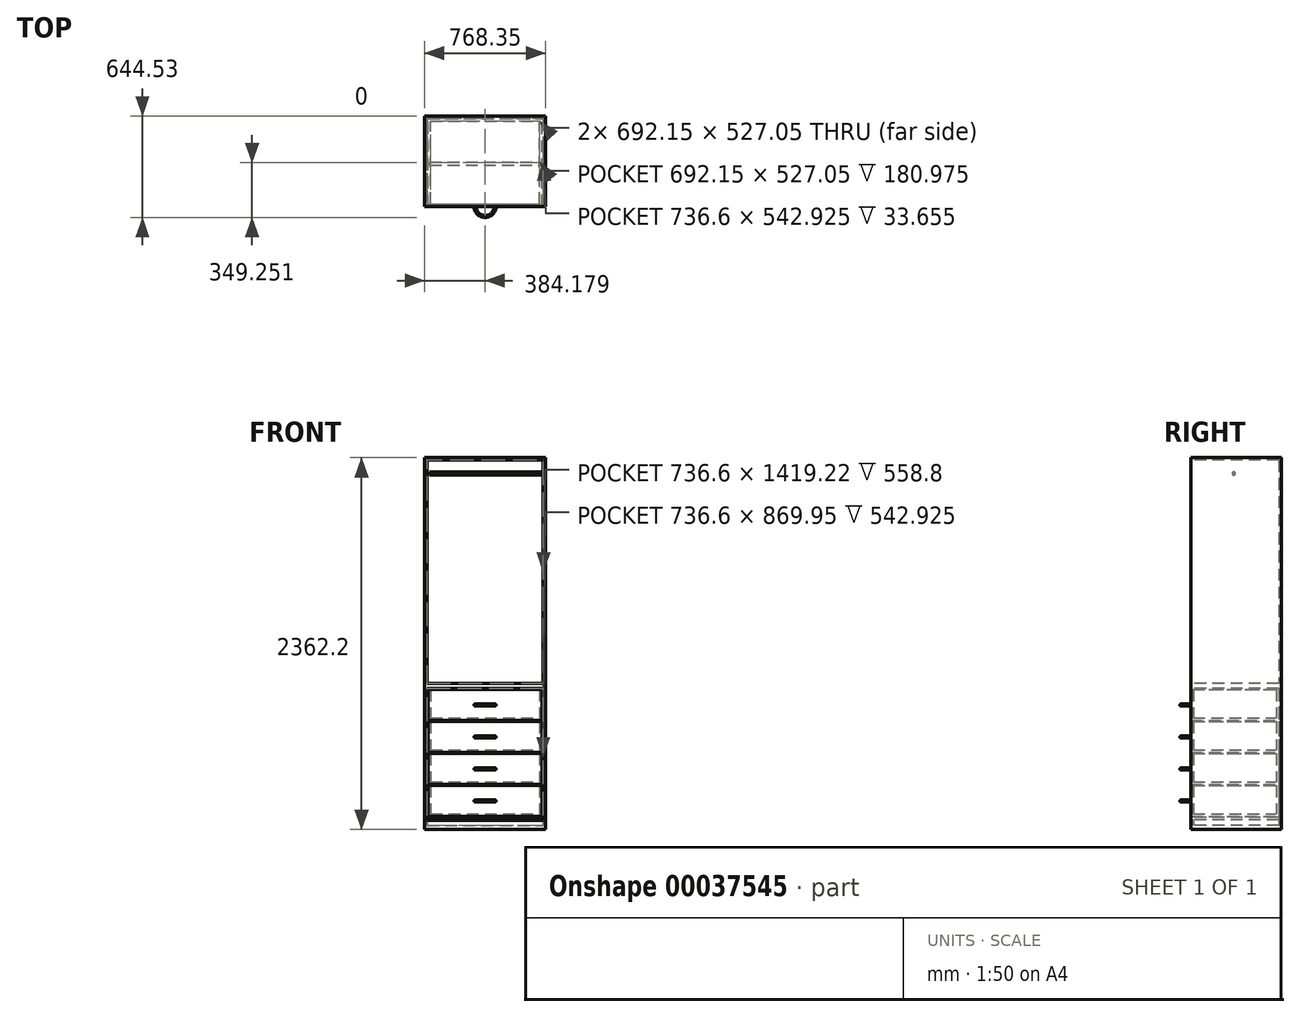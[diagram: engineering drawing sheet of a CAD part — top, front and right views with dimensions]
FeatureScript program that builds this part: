
annotation { "Feature Type Name" : "Feature", "Feature Type Description" : "" }
export const myFeature = defineFeature(function(context is Context, id is Id, definition is map)
    precondition{}
    {
        {
            var Q0;
            Q0=qCreatedBy(makeId("Top.planeOp"),FACE);
            var sketch = newSketch(context, id + "F0", { "sketchPlane" : qUnion([Q0])});
            skLineSegment(sketch, "E0.bottom", {"start": v(-263.66, 331.87) * mm, "end": v(504.7, 331.87) * mm});
            skLineSegment(sketch, "E0.top", {"start": v(-263.66, -242.8) * mm, "end": v(504.7, -242.8) * mm});
            skLineSegment(sketch, "E0.left", {"start": v(-263.66, 331.87) * mm, "end": v(-263.66, -242.8) * mm});
            skLineSegment(sketch, "E0.right", {"start": v(504.7, 331.87) * mm, "end": v(504.7, -242.8) * mm});
            skLineSegment(sketch, "E1.0", {"start": v(488.82, 317.59) * mm, "end": v(488.82, -257.09) * mm});
            skLineSegment(sketch, "E2.0", {"start": v(-247.78, 316) * mm, "end": v(504.7, 316) * mm});
            skLineSegment(sketch, "E3.0", {"start": v(-247.78, 331.87) * mm, "end": v(-247.78, -242.8) * mm});
            skLineSegment(sketch, "E4.0", {"start": v(-247.78, -226.93) * mm, "end": v(504.7, -226.93) * mm});
            skLineSegment(sketch, "E5.bottom", {"start": v(-263.66, 331.87) * mm, "end": v(-545.72, 331.87) * mm});
            skLineSegment(sketch, "E5.top", {"start": v(-263.66, -242.8) * mm, "end": v(-545.72, -242.8) * mm});
            skLineSegment(sketch, "E5.right", {"start": v(-545.72, 331.87) * mm, "end": v(-545.72, -242.8) * mm});
            skSolve(sketch);
        }
        {
            var Q0;
            {var subQ0=sQuery(id+"F0.wireOp",EDGE,"E2.0");var subQ3=sQuery(id+"F0.wireOp",EDGE,"E0.left");var subQ4=makeQuery(id+"F0.imprint","INTERSECT",VERTEX,{"derivedFrom":[subQ3,subQ0]});Q0=makeQuery(id+"F0.imprint","IMPRINT",FACE,{"disambiguationData":[TD([[makeQuery(id+"F0.imprint","IMPRINT",EDGE,{"disambiguationData":[TD([[subQ4,-1.0]])],"derivedFrom":subQ3}),1.0]])]});}
            var Q1;
            {var subQ3=sQuery(id+"F0.wireOp",EDGE,"E0.left");var subQ5=sQuery(id+"F0.wireOp",EDGE,"E0.bottom");var subQ6=makeQuery(id+"F0.imprint","INTERSECT",VERTEX,{"derivedFrom":[subQ5,subQ3]});Q1=makeQuery(id+"F0.imprint","IMPRINT",FACE,{"disambiguationData":[TD([[makeQuery(id+"F0.imprint","IMPRINT",EDGE,{"disambiguationData":[TD([[subQ6,-1.0]])],"derivedFrom":subQ5}),-1.0]])]});}
            var Q2;
            {var subQ3=sQuery(id+"F0.wireOp",EDGE,"E0.left");var subQ5=sQuery(id+"F0.wireOp",EDGE,"E0.top");var subQ7=makeQuery(id+"F0.imprint","INTERSECT",VERTEX,{"derivedFrom":[subQ5,subQ3]});Q2=makeQuery(id+"F0.imprint","IMPRINT",FACE,{"disambiguationData":[TD([[makeQuery(id+"F0.imprint","IMPRINT",EDGE,{"disambiguationData":[TD([[subQ7,-1.0]])],"derivedFrom":subQ5}),1.0]])]});}
            extrude(context, id + "F1", {"entities" : qUnion([Q0, Q1, Q2]), "depth" : 2362.2 * mm});
        }
        {
            var Q0;
            {var subQ0=sQuery(id+"F0.wireOp",EDGE,"E1.0");var subQ3=sQuery(id+"F0.wireOp",EDGE,"E0.bottom");var subQ4=makeQuery(id+"F0.imprint","INTERSECT",VERTEX,{"derivedFrom":[subQ3,subQ0]});Q0=makeQuery(id+"F0.imprint","IMPRINT",FACE,{"disambiguationData":[TD([[makeQuery(id+"F0.imprint","IMPRINT",EDGE,{"disambiguationData":[TD([[subQ4,1.0]])],"derivedFrom":subQ3}),-1.0]])]});}
            extrude(context, id + "F2", {"entities" : qUnion([Q0]), "operationType" : NewBodyOperationType.ADD, "depth" : 2362.2 * mm});
        }
        {
            var Q0;
            {var subQ3=sQuery(id+"F0.wireOp",EDGE,"E0.bottom");var subQ5=sQuery(id+"F0.wireOp",EDGE,"E0.right");var subQ7=makeQuery(id+"F0.imprint","INTERSECT",VERTEX,{"derivedFrom":[subQ3,subQ5]});Q0=makeQuery(id+"F0.imprint","IMPRINT",FACE,{"disambiguationData":[TD([[makeQuery(id+"F0.imprint","IMPRINT",EDGE,{"disambiguationData":[TD([[subQ7,1.0]])],"derivedFrom":subQ3}),-1.0]])]});}
            var Q1;
            {var subQ3=sQuery(id+"F0.wireOp",EDGE,"E0.right");var subQ5=sQuery(id+"F0.wireOp",EDGE,"E2.0");var subQ7=makeQuery(id+"F0.imprint","INTERSECT",VERTEX,{"derivedFrom":[subQ3,subQ5]});Q1=makeQuery(id+"F0.imprint","IMPRINT",FACE,{"disambiguationData":[TD([[makeQuery(id+"F0.imprint","IMPRINT",EDGE,{"disambiguationData":[TD([[subQ7,-1.0]])],"derivedFrom":subQ3}),-1.0]])]});}
            var Q2;
            {var subQ3=sQuery(id+"F0.wireOp",EDGE,"E0.right");var subQ5=sQuery(id+"F0.wireOp",EDGE,"E0.top");var subQ7=makeQuery(id+"F0.imprint","INTERSECT",VERTEX,{"derivedFrom":[subQ5,subQ3]});Q2=makeQuery(id+"F0.imprint","IMPRINT",FACE,{"disambiguationData":[TD([[makeQuery(id+"F0.imprint","IMPRINT",EDGE,{"disambiguationData":[TD([[subQ7,1.0]])],"derivedFrom":subQ5}),1.0]])]});}
            extrude(context, id + "F3", {"entities" : qUnion([Q0, Q1, Q2]), "operationType" : NewBodyOperationType.ADD, "depth" : 2362.2 * mm});
        }
        {
            var Q0;
            {var subQ0=sQuery(id+"F0.wireOp",EDGE,"E1.0");var subQ3=sQuery(id+"F0.wireOp",EDGE,"E0.top");var subQ4=makeQuery(id+"F0.imprint","INTERSECT",VERTEX,{"derivedFrom":[subQ3,subQ0]});Q0=makeQuery(id+"F0.imprint","IMPRINT",FACE,{"disambiguationData":[TD([[makeQuery(id+"F0.imprint","IMPRINT",EDGE,{"disambiguationData":[TD([[subQ4,1.0]])],"derivedFrom":subQ3}),1.0]])]});}
            extrude(context, id + "F4", {"entities" : qUnion([Q0]), "operationType" : NewBodyOperationType.ADD, "depth" : 59.05 * mm});
        }
        {
            var Q0;
            {var subQ3=sQuery(id+"F0.wireOp",EDGE,"E1.0");var subQ5=sQuery(id+"F0.wireOp",EDGE,"E2.0");var subQ7=makeQuery(id+"F0.imprint","INTERSECT",VERTEX,{"derivedFrom":[subQ3,subQ5]});Q0=makeQuery(id+"F0.imprint","IMPRINT",FACE,{"disambiguationData":[TD([[makeQuery(id+"F0.imprint","IMPRINT",EDGE,{"disambiguationData":[TD([[subQ7,-1.0]])],"derivedFrom":subQ3}),-1.0]])]});}
            var Q1;
            {var subQ0=sQuery(id+"F0.wireOp",EDGE,"E1.0");var subQ3=sQuery(id+"F0.wireOp",EDGE,"E0.top");var subQ4=makeQuery(id+"F0.imprint","INTERSECT",VERTEX,{"derivedFrom":[subQ3,subQ0]});Q1=makeQuery(id+"F0.imprint","IMPRINT",FACE,{"disambiguationData":[TD([[makeQuery(id+"F0.imprint","IMPRINT",EDGE,{"disambiguationData":[TD([[subQ4,1.0]])],"derivedFrom":subQ3}),1.0]])]});}
            extrude(context, id + "F5", {"entities" : qUnion([Q0, Q1]), "depth" : 76.2 * mm, "hasSecondDirection" : true, "secondDirectionOppositeDirection" : false, "secondDirectionDepth" : 59.69 * mm});
        }
        {
            var Q0;
            Q0=makeQuery(id+"F5.opExtrude","CAP_FACE",FACE,{"disambiguationData":[OSD([sQuery(id+"F0.wireOp",EDGE,"E0.top"),sQuery(id+"F0.wireOp",EDGE,"E1.0"),sQuery(id+"F0.wireOp",EDGE,"E2.0"),sQuery(id+"F0.wireOp",EDGE,"E3.0")])],"isStart":false});
            var sketch = newSketch(context, id + "F6", { "sketchPlane" : qUnion([Q0])});
            skLineSegment(sketch, "E6.bottom", {"start": v(-247.78, -242.8) * mm, "end": v(488.82, -242.8) * mm});
            skLineSegment(sketch, "E6.top", {"start": v(-247.78, 316) * mm, "end": v(488.82, 316) * mm});
            skLineSegment(sketch, "E6.left", {"start": v(-247.78, -242.8) * mm, "end": v(-247.78, 316) * mm});
            skLineSegment(sketch, "E6.right", {"start": v(488.82, -242.8) * mm, "end": v(488.82, 316) * mm});
            skLineSegment(sketch, "E7.0", {"start": v(-241.43, -242.8) * mm, "end": v(-241.43, 316) * mm});
            skLineSegment(sketch, "E8.0", {"start": v(482.47, -242.8) * mm, "end": v(482.47, 316) * mm});
            skLineSegment(sketch, "E9.0", {"start": v(466.6, -242.8) * mm, "end": v(466.6, 316) * mm});
            skLineSegment(sketch, "E10.0", {"start": v(-225.56, -242.8) * mm, "end": v(-225.56, 316) * mm});
            skLineSegment(sketch, "E11.0", {"start": v(-247.78, 300.12) * mm, "end": v(488.82, 300.12) * mm});
            skLineSegment(sketch, "E12.0", {"start": v(-247.78, -226.93) * mm, "end": v(488.82, -226.93) * mm});
            skSolve(sketch);
        }
        {
            var Q0;
            {var subQ0=sQuery(id+"F6.wireOp",EDGE,"E12.0");var subQ3=sQuery(id+"F6.wireOp",EDGE,"E7.0");var subQ4=makeQuery(id+"F6.imprint","INTERSECT",VERTEX,{"derivedFrom":[subQ3,subQ0]});Q0=makeQuery(id+"F6.imprint","IMPRINT",FACE,{"disambiguationData":[TD([[makeQuery(id+"F6.imprint","IMPRINT",EDGE,{"disambiguationData":[TD([[subQ4,-1.0]])],"derivedFrom":subQ3}),-1.0]])]});}
            var Q1;
            {var subQ3=sQuery(id+"F6.wireOp",EDGE,"E7.0");var subQ5=sQuery(id+"F6.wireOp",EDGE,"E6.top");var subQ7=makeQuery(id+"F6.imprint","INTERSECT",VERTEX,{"derivedFrom":[subQ5,subQ3]});Q1=makeQuery(id+"F6.imprint","IMPRINT",FACE,{"disambiguationData":[TD([[makeQuery(id+"F6.imprint","IMPRINT",EDGE,{"disambiguationData":[TD([[subQ7,-1.0]])],"derivedFrom":subQ5}),-1.0]])]});}
            var Q2;
            {var subQ3=sQuery(id+"F6.wireOp",EDGE,"E9.0");var subQ5=sQuery(id+"F6.wireOp",EDGE,"E6.top");var subQ7=makeQuery(id+"F6.imprint","INTERSECT",VERTEX,{"derivedFrom":[subQ5,subQ3]});Q2=makeQuery(id+"F6.imprint","IMPRINT",FACE,{"disambiguationData":[TD([[makeQuery(id+"F6.imprint","IMPRINT",EDGE,{"disambiguationData":[TD([[subQ7,1.0]])],"derivedFrom":subQ5}),-1.0]])]});}
            var Q3;
            {var subQ3=sQuery(id+"F6.wireOp",EDGE,"E6.bottom");var subQ5=sQuery(id+"F6.wireOp",EDGE,"E7.0");var subQ7=makeQuery(id+"F6.imprint","INTERSECT",VERTEX,{"derivedFrom":[subQ3,subQ5]});Q3=makeQuery(id+"F6.imprint","IMPRINT",FACE,{"disambiguationData":[TD([[makeQuery(id+"F6.imprint","IMPRINT",EDGE,{"disambiguationData":[TD([[subQ7,-1.0]])],"derivedFrom":subQ3}),1.0]])]});}
            var Q4;
            {var subQ3=sQuery(id+"F6.wireOp",EDGE,"E6.bottom");var subQ5=sQuery(id+"F6.wireOp",EDGE,"E9.0");var subQ7=makeQuery(id+"F6.imprint","INTERSECT",VERTEX,{"derivedFrom":[subQ3,subQ5]});Q4=makeQuery(id+"F6.imprint","IMPRINT",FACE,{"disambiguationData":[TD([[makeQuery(id+"F6.imprint","IMPRINT",EDGE,{"disambiguationData":[TD([[subQ7,1.0]])],"derivedFrom":subQ3}),1.0]])]});}
            var Q5;
            {var subQ3=sQuery(id+"F6.wireOp",EDGE,"E8.0");var subQ5=sQuery(id+"F6.wireOp",EDGE,"E6.top");var subQ7=makeQuery(id+"F6.imprint","INTERSECT",VERTEX,{"derivedFrom":[subQ5,subQ3]});Q5=makeQuery(id+"F6.imprint","IMPRINT",FACE,{"disambiguationData":[TD([[makeQuery(id+"F6.imprint","IMPRINT",EDGE,{"disambiguationData":[TD([[subQ7,1.0]])],"derivedFrom":subQ5}),-1.0]])]});}
            var Q6;
            {var subQ0=sQuery(id+"F6.wireOp",EDGE,"E12.0");var subQ3=sQuery(id+"F6.wireOp",EDGE,"E8.0");var subQ4=makeQuery(id+"F6.imprint","INTERSECT",VERTEX,{"derivedFrom":[subQ3,subQ0]});Q6=makeQuery(id+"F6.imprint","IMPRINT",FACE,{"disambiguationData":[TD([[makeQuery(id+"F6.imprint","IMPRINT",EDGE,{"disambiguationData":[TD([[subQ4,-1.0]])],"derivedFrom":subQ3}),1.0]])]});}
            var Q7;
            {var subQ3=sQuery(id+"F6.wireOp",EDGE,"E6.bottom");var subQ5=sQuery(id+"F6.wireOp",EDGE,"E8.0");var subQ7=makeQuery(id+"F6.imprint","INTERSECT",VERTEX,{"derivedFrom":[subQ3,subQ5]});Q7=makeQuery(id+"F6.imprint","IMPRINT",FACE,{"disambiguationData":[TD([[makeQuery(id+"F6.imprint","IMPRINT",EDGE,{"disambiguationData":[TD([[subQ7,1.0]])],"derivedFrom":subQ3}),1.0]])]});}
            extrude(context, id + "F7", {"entities" : qUnion([Q0, Q1, Q2, Q3, Q4, Q5, Q6, Q7]), "depth" : 203.2 * mm, "hasSecondDirection" : true, "secondDirectionOppositeDirection" : false, "secondDirectionDepth" : 6.35 * mm});
        }
        {
            var Q0;
            {var subQ0=sQuery(id+"F6.wireOp",EDGE,"E12.0");var subQ3=sQuery(id+"F6.wireOp",EDGE,"E9.0");var subQ4=makeQuery(id+"F6.imprint","INTERSECT",VERTEX,{"derivedFrom":[subQ3,subQ0]});Q0=makeQuery(id+"F6.imprint","IMPRINT",FACE,{"disambiguationData":[TD([[makeQuery(id+"F6.imprint","IMPRINT",EDGE,{"disambiguationData":[TD([[subQ4,-1.0]])],"derivedFrom":subQ3}),1.0]])]});}
            extrude(context, id + "F8", {"entities" : qUnion([Q0]), "operationType" : NewBodyOperationType.ADD, "depth" : 22.22 * mm, "hasSecondDirection" : true, "secondDirectionOppositeDirection" : false, "secondDirectionDepth" : 6.35 * mm});
        }
        {
            var Q0;
            Q0=makeQuery(id+"F7.opExtrude","SWEPT_BODY",BODY,{"disambiguationData":[OSD([sQuery(id+"F6.wireOp",EDGE,"E6.bottom"),sQuery(id+"F6.wireOp",EDGE,"E6.top"),sQuery(id+"F6.wireOp",EDGE,"E7.0"),sQuery(id+"F6.wireOp",EDGE,"E8.0"),sQuery(id+"F6.wireOp",EDGE,"E9.0"),sQuery(id+"F6.wireOp",EDGE,"E10.0"),sQuery(id+"F6.wireOp",EDGE,"E11.0"),sQuery(id+"F6.wireOp",EDGE,"E12.0")])]});
            transform(context, id + "F9", {"entities" : qUnion([Q0]), "transformType" : TransformType.TRANSLATION_3D, "dx" : 0 * mm, "dy" : 0 * mm, "dz" : 203.2 * mm, "makeCopy" : true});
        }
        {
            var Q0;
            Q0=makeQuery(id+"F9.opPattern","COPY",BODY,{"derivedFrom":makeQuery(id+"F7.opExtrude","SWEPT_BODY",BODY,{"disambiguationData":[OSD([sQuery(id+"F6.wireOp",EDGE,"E6.bottom"),sQuery(id+"F6.wireOp",EDGE,"E6.top"),sQuery(id+"F6.wireOp",EDGE,"E7.0"),sQuery(id+"F6.wireOp",EDGE,"E8.0"),sQuery(id+"F6.wireOp",EDGE,"E9.0"),sQuery(id+"F6.wireOp",EDGE,"E10.0"),sQuery(id+"F6.wireOp",EDGE,"E11.0"),sQuery(id+"F6.wireOp",EDGE,"E12.0")])]}),"instanceName":"1"});
            transform(context, id + "F10", {"entities" : qUnion([Q0]), "transformType" : TransformType.TRANSLATION_3D, "dx" : 0 * mm, "dy" : 0 * mm, "dz" : 203.2 * mm, "makeCopy" : true});
        }
        {
            var Q0;
            Q0=makeQuery(id+"F10.opPattern","COPY",BODY,{"derivedFrom":makeQuery(id+"F9.opPattern","COPY",BODY,{"derivedFrom":makeQuery(id+"F7.opExtrude","SWEPT_BODY",BODY,{"disambiguationData":[OSD([sQuery(id+"F6.wireOp",EDGE,"E6.bottom"),sQuery(id+"F6.wireOp",EDGE,"E6.top"),sQuery(id+"F6.wireOp",EDGE,"E7.0"),sQuery(id+"F6.wireOp",EDGE,"E8.0"),sQuery(id+"F6.wireOp",EDGE,"E9.0"),sQuery(id+"F6.wireOp",EDGE,"E10.0"),sQuery(id+"F6.wireOp",EDGE,"E11.0"),sQuery(id+"F6.wireOp",EDGE,"E12.0")])]}),"instanceName":"1"}),"instanceName":"1"});
            transform(context, id + "F11", {"entities" : qUnion([Q0]), "transformType" : TransformType.TRANSLATION_3D, "dx" : 0 * mm, "dy" : 0 * mm, "dz" : 203.2 * mm, "makeCopy" : true});
        }
        {
            var Q0;
            {var subQ3=sQuery(id+"F0.wireOp",EDGE,"E1.0");var subQ5=sQuery(id+"F0.wireOp",EDGE,"E2.0");var subQ7=makeQuery(id+"F0.imprint","INTERSECT",VERTEX,{"derivedFrom":[subQ3,subQ5]});Q0=makeQuery(id+"F0.imprint","IMPRINT",FACE,{"disambiguationData":[TD([[makeQuery(id+"F0.imprint","IMPRINT",EDGE,{"disambiguationData":[TD([[subQ7,-1.0]])],"derivedFrom":subQ3}),-1.0]])]});}
            var Q1;
            {var subQ0=sQuery(id+"F0.wireOp",EDGE,"E1.0");var subQ3=sQuery(id+"F0.wireOp",EDGE,"E0.top");var subQ4=makeQuery(id+"F0.imprint","INTERSECT",VERTEX,{"derivedFrom":[subQ3,subQ0]});Q1=makeQuery(id+"F0.imprint","IMPRINT",FACE,{"disambiguationData":[TD([[makeQuery(id+"F0.imprint","IMPRINT",EDGE,{"disambiguationData":[TD([[subQ4,1.0]])],"derivedFrom":subQ3}),1.0]])]});}
            extrude(context, id + "F12", {"entities" : qUnion([Q0, Q1]), "operationType" : NewBodyOperationType.ADD, "depth" : 25.4 * mm});
        }
        {
            var Q0;
            {var subQ3=sQuery(id+"F0.wireOp",EDGE,"E1.0");var subQ5=sQuery(id+"F0.wireOp",EDGE,"E2.0");var subQ7=makeQuery(id+"F0.imprint","INTERSECT",VERTEX,{"derivedFrom":[subQ3,subQ5]});Q0=makeQuery(id+"F0.imprint","IMPRINT",FACE,{"disambiguationData":[TD([[makeQuery(id+"F0.imprint","IMPRINT",EDGE,{"disambiguationData":[TD([[subQ7,-1.0]])],"derivedFrom":subQ3}),-1.0]])]});}
            var Q1;
            {var subQ0=sQuery(id+"F0.wireOp",EDGE,"E1.0");var subQ3=sQuery(id+"F0.wireOp",EDGE,"E0.top");var subQ4=makeQuery(id+"F0.imprint","INTERSECT",VERTEX,{"derivedFrom":[subQ3,subQ0]});Q1=makeQuery(id+"F0.imprint","IMPRINT",FACE,{"disambiguationData":[TD([[makeQuery(id+"F0.imprint","IMPRINT",EDGE,{"disambiguationData":[TD([[subQ4,1.0]])],"derivedFrom":subQ3}),1.0]])]});}
            extrude(context, id + "F13", {"entities" : qUnion([Q0, Q1]), "operationType" : NewBodyOperationType.ADD, "depth" : 911.22 * mm, "hasSecondDirection" : true, "secondDirectionOppositeDirection" : false, "secondDirectionDepth" : 895.35 * mm});
        }
        {
            var Q0;
            {var subQ3=sQuery(id+"F0.wireOp",EDGE,"E1.0");var subQ5=sQuery(id+"F0.wireOp",EDGE,"E2.0");var subQ7=makeQuery(id+"F0.imprint","INTERSECT",VERTEX,{"derivedFrom":[subQ3,subQ5]});Q0=makeQuery(id+"F0.imprint","IMPRINT",FACE,{"disambiguationData":[TD([[makeQuery(id+"F0.imprint","IMPRINT",EDGE,{"disambiguationData":[TD([[subQ7,-1.0]])],"derivedFrom":subQ3}),-1.0]])]});}
            var Q1;
            {var subQ0=sQuery(id+"F0.wireOp",EDGE,"E1.0");var subQ3=sQuery(id+"F0.wireOp",EDGE,"E0.top");var subQ4=makeQuery(id+"F0.imprint","INTERSECT",VERTEX,{"derivedFrom":[subQ3,subQ0]});Q1=makeQuery(id+"F0.imprint","IMPRINT",FACE,{"disambiguationData":[TD([[makeQuery(id+"F0.imprint","IMPRINT",EDGE,{"disambiguationData":[TD([[subQ4,1.0]])],"derivedFrom":subQ3}),1.0]])]});}
            extrude(context, id + "F14", {"entities" : qUnion([Q0, Q1]), "operationType" : NewBodyOperationType.ADD, "depth" : 927.1 * mm, "hasSecondDirection" : true, "secondDirectionOppositeDirection" : false, "secondDirectionDepth" : 909.96 * mm});
        }
        {
            var Q0;
            {var subQ0=sQuery(id+"F0.wireOp",EDGE,"E1.0");var subQ3=sQuery(id+"F0.wireOp",EDGE,"E0.top");var subQ4=makeQuery(id+"F0.imprint","INTERSECT",VERTEX,{"derivedFrom":[subQ3,subQ0]});Q0=makeQuery(id+"F0.imprint","IMPRINT",FACE,{"disambiguationData":[TD([[makeQuery(id+"F0.imprint","IMPRINT",EDGE,{"disambiguationData":[TD([[subQ4,1.0]])],"derivedFrom":subQ3}),1.0]])]});}
            var Q1;
            {var subQ3=sQuery(id+"F0.wireOp",EDGE,"E1.0");var subQ5=sQuery(id+"F0.wireOp",EDGE,"E2.0");var subQ7=makeQuery(id+"F0.imprint","INTERSECT",VERTEX,{"derivedFrom":[subQ3,subQ5]});Q1=makeQuery(id+"F0.imprint","IMPRINT",FACE,{"disambiguationData":[TD([[makeQuery(id+"F0.imprint","IMPRINT",EDGE,{"disambiguationData":[TD([[subQ7,-1.0]])],"derivedFrom":subQ3}),-1.0]])]});}
            extrude(context, id + "F15", {"entities" : qUnion([Q0, Q1]), "operationType" : NewBodyOperationType.ADD, "depth" : 2362.2 * mm, "hasSecondDirection" : true, "secondDirectionOppositeDirection" : false, "secondDirectionDepth" : 2346.32 * mm});
        }
        {
            var Q0;
            Q0=makeQuery(id+"F7.opExtrude","SWEPT_FACE",FACE,{"disambiguationData":[OSD([sQuery(id+"F6.wireOp",EDGE,"E6.bottom")])]});
            var sketch = newSketch(context, id + "F16", { "sketchPlane" : qUnion([Q0])});
            skLineSegment(sketch, "E13", {"start": v(120.52, 279.4) * mm, "end": v(120.52, 82.55) * mm});
            skCircle(sketch, "E14", {"center": v(57.02, 180.98) * mm, "radius": 6.35 * mm});
            skPoint(sketch, "E15.orphan", {"position": v(57.02, 82.55) * mm});
            skPoint(sketch, "E16.0.start.orphan", {"position": v(57.02, 279.4) * mm});
            skSolve(sketch);
        }
        {
            var Q0;
            Q0=makeQuery(id+"F16.imprint","IMPRINT",FACE,{"disambiguationData":[TD([[makeQuery(id+"F16.imprint","IMPRINT",EDGE,{"derivedFrom":sQuery(id+"F16.wireOp",EDGE,"E14")}),1.0]])]});
            var Q1;
            Q1=sQuery(id+"F16.wireOp",EDGE,"E13");
            revolve(context, id + "F17", {"entities" : qUnion([Q0]), "axis" : qUnion([Q1]), "revolveType" : RevolveType.ONE_DIRECTION, "oppositeDirection" : true, "angle" : 180 * degree});
        }
        {
            var Q0;
            Q0=makeQuery(id+"F17.opRevolve","SWEPT_BODY",BODY,{"disambiguationData":[OSD([sQuery(id+"F16.wireOp",EDGE,"E14")])]});
            transform(context, id + "F18", {"entities" : qUnion([Q0]), "transformType" : TransformType.TRANSLATION_3D, "dx" : 0 * mm, "dy" : 0 * mm, "dz" : 203.2 * mm, "makeCopy" : true});
        }
        {
            var Q0;
            Q0=makeQuery(id+"F18.opPattern","COPY",BODY,{"derivedFrom":makeQuery(id+"F17.opRevolve","SWEPT_BODY",BODY,{"disambiguationData":[OSD([sQuery(id+"F16.wireOp",EDGE,"E14")])]}),"instanceName":"1"});
            transform(context, id + "F19", {"entities" : qUnion([Q0]), "transformType" : TransformType.TRANSLATION_3D, "dx" : 0 * mm, "dy" : 0 * mm, "dz" : 203.2 * mm, "makeCopy" : true});
        }
        {
            var Q0;
            Q0=makeQuery(id+"F19.opPattern","COPY",BODY,{"derivedFrom":makeQuery(id+"F18.opPattern","COPY",BODY,{"derivedFrom":makeQuery(id+"F17.opRevolve","SWEPT_BODY",BODY,{"disambiguationData":[OSD([sQuery(id+"F16.wireOp",EDGE,"E14")])]}),"instanceName":"1"}),"instanceName":"1"});
            transform(context, id + "F20", {"entities" : qUnion([Q0]), "transformType" : TransformType.TRANSLATION_3D, "dx" : 0 * mm, "dy" : 0 * mm, "dz" : 203.2 * mm, "makeCopy" : true});
        }
        {
            var Q0;
            Q0=makeQuery(id+"F3.opExtrude","SWEPT_FACE",FACE,{"disambiguationData":[OSD([sQuery(id+"F0.wireOp",EDGE,"E0.right")])]});
            var sketch = newSketch(context, id + "F21", { "sketchPlane" : qUnion([Q0])});
            skPoint(sketch, "E17.start.orphan", {"position": v(44.53, 2362.2) * mm});
            skCircle(sketch, "E18", {"center": v(30.25, 2260.6) * mm, "radius": 9.52 * mm});
            skSolve(sketch);
        }
        {
            var Q0;
            Q0=makeQuery(id+"F21.imprint","IMPRINT",FACE,{"disambiguationData":[TD([[makeQuery(id+"F21.imprint","IMPRINT",EDGE,{"derivedFrom":sQuery(id+"F21.wireOp",EDGE,"E18")}),1.0]])]});
            extrude(context, id + "F22", {"entities" : qUnion([Q0]), "oppositeDirection" : true, "depth" : 736.6 * mm, "hasSecondDirection" : true, "secondDirectionOppositeDirection" : true, "secondDirectionDepth" : 15.88 * mm});
        }
    });
